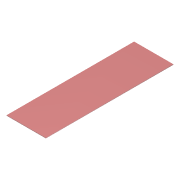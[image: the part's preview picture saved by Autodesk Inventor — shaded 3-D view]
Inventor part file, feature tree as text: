
AUTODESK INVENTOR PART (.ipt)
format: ipt  version: 2016 (Build 200138000, 138)  size: 69,632 bytes
history: native  units: mm
features: extrude x1, sketch x1
ambient origin geometry x8: Origin, YZ Plane, XZ Plane, XY Plane, X Axis, Y Axis, Z Axis, Center Point
bodies: Volumenkörper1 (feature_tree)
feature tree (2):
  extrude  "Extrusion1"  Depth=650.0mm
  sketch  "Skizze1"  dims[d0=200.0mm d1=650.0mm d2=3.0mm d3=0.0mm]
